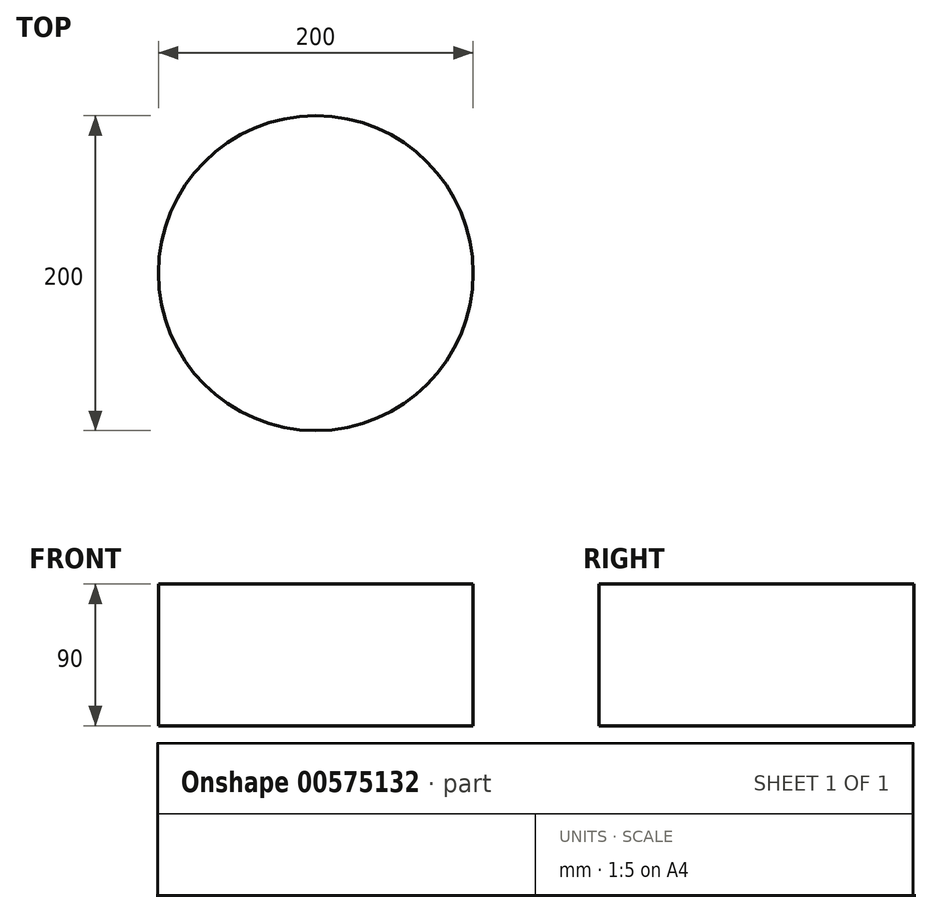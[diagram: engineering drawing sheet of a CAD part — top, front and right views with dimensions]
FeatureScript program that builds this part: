
annotation { "Feature Type Name" : "Feature", "Feature Type Description" : "" }
export const myFeature = defineFeature(function(context is Context, id is Id, definition is map)
    precondition{}
    {
        {
            var Q0;
            Q0=qCreatedBy(makeId("Top.planeOp"),FACE);
            var sketch = newSketch(context, id + "F0", { "sketchPlane" : qUnion([Q0])});
            skCircle(sketch, "E0", {"center": v(0, 0) * mm, "radius": 100 * mm});
            skSolve(sketch);
        }
        {
            var Q0;
            Q0=makeQuery(id+"F0.imprint","IMPRINT",FACE,{"disambiguationData":[TD([[makeQuery(id+"F0.imprint","IMPRINT",EDGE,{"derivedFrom":sQuery(id+"F0.wireOp",EDGE,"E0")}),1.0]])]});
            extrude(context, id + "F1", {"entities" : qUnion([Q0]), "endBound" : BoundingType.SYMMETRIC, "depth" : 90 * mm, "offsetDistance" : 25 * mm});
        }
    });
